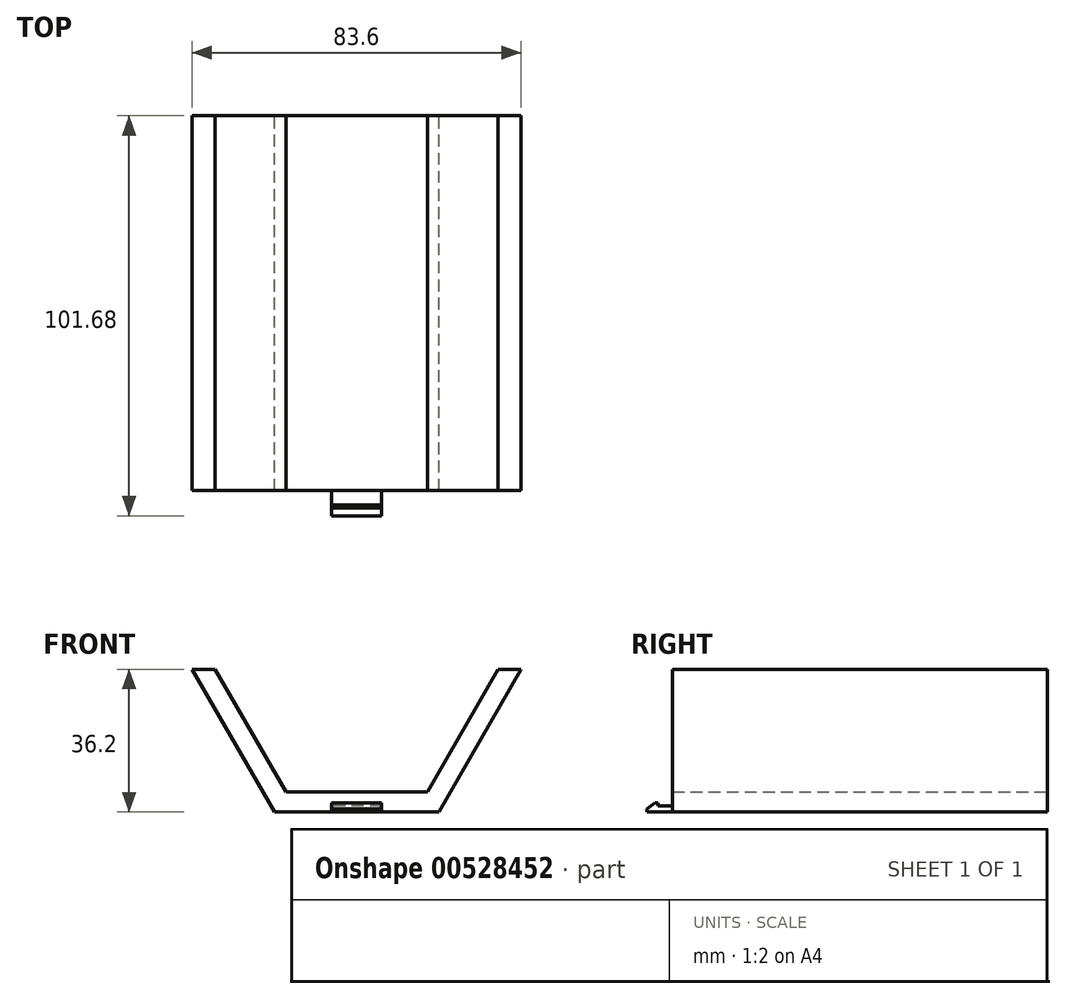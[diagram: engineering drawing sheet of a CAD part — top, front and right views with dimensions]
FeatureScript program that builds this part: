
annotation { "Feature Type Name" : "Feature", "Feature Type Description" : "" }
export const myFeature = defineFeature(function(context is Context, id is Id, definition is map)
    precondition{}
    {
        {
            var Q0;
            Q0=qCreatedBy(makeId("Front.planeOp"),FACE);
            var sketch = newSketch(context, id + "F0", { "sketchPlane" : qUnion([Q0])});
            skCircle(sketch, "E0.cCircle", {"center": v(0, 36.2) * mm, "radius": 36.2 * mm, "construction": true});
            skLineSegment(sketch, "E0.0", {"start": v(41.8, 36.2) * mm, "end": v(20.9, 0) * mm});
            skLineSegment(sketch, "E0.1", {"start": v(20.9, 0) * mm, "end": v(-20.9, 0) * mm});
            skLineSegment(sketch, "E0.2", {"start": v(-20.9, 0) * mm, "end": v(-41.8, 36.2) * mm});
            skLineSegment(sketch, "E0.3", {"start": v(-41.8, 36.2) * mm, "end": v(-20.9, 72.4) * mm, "construction": true});
            skLineSegment(sketch, "E0.4", {"start": v(-20.9, 72.4) * mm, "end": v(20.9, 72.4) * mm, "construction": true});
            skLineSegment(sketch, "E0.5", {"start": v(20.9, 72.39) * mm, "end": v(41.8, 36.2) * mm, "construction": true});
            skPoint(sketch, "E0.0.midPoint", {"position": v(31.35, 18.1) * mm});
            skLineSegment(sketch, "E1.0", {"start": v(-17.96, 5.08) * mm, "end": v(-35.93, 36.2) * mm});
            skLineSegment(sketch, "E1.1", {"start": v(-18.5, 67.31) * mm, "end": v(-17.96, 67.31) * mm});
            skLineSegment(sketch, "E1.2", {"start": v(17.7, 67.77) * mm, "end": v(17.96, 67.3) * mm});
            skLineSegment(sketch, "E1.3", {"start": v(-36.2, 35.74) * mm, "end": v(-35.93, 36.2) * mm});
            skLineSegment(sketch, "E1.4", {"start": v(35.93, 36.2) * mm, "end": v(17.96, 5.08) * mm});
            skLineSegment(sketch, "E1.5", {"start": v(17.96, 5.08) * mm, "end": v(-17.96, 5.08) * mm});
            skLineSegment(sketch, "E2", {"start": v(-35.93, 36.2) * mm, "end": v(-41.8, 36.2) * mm});
            skLineSegment(sketch, "E3", {"start": v(41.8, 36.2) * mm, "end": v(35.93, 36.2) * mm});
            skLineSegment(sketch, "E4.trimOffspring", {"start": v(35.93, 36.2) * mm, "end": v(36.2, 35.74) * mm});
            skLineSegment(sketch, "E5.trimOffspring", {"start": v(17.96, 67.31) * mm, "end": v(18.5, 67.31) * mm});
            skLineSegment(sketch, "E6.trimOffspring", {"start": v(-17.96, 67.31) * mm, "end": v(-17.7, 67.77) * mm});
            skSolve(sketch);
        }
        {
            var Q0;
            Q0 = qSketchRegion(id + "F0", true);
            extrude(context, id + "F1", {"entities" : qUnion([Q0]), "endBound" : BoundingType.SYMMETRIC, "depth" : 95.25 * mm, "offsetDistance" : 25.4 * mm});
        }
        {
            var Q0;
            Q0=qCreatedBy(makeId("Right.planeOp"),FACE);
            var sketch = newSketch(context, id + "F2", { "sketchPlane" : qUnion([Q0])});
            skLineSegment(sketch, "E7", {"start": v(-51.3, 1.52) * mm, "end": v(-51.3, 2.29) * mm});
            skLineSegment(sketch, "E8", {"start": v(-51.3, 2.29) * mm, "end": v(-52.07, 2.29) * mm});
            skLineSegment(sketch, "E9", {"start": v(-52.07, 2.29) * mm, "end": v(-54.06, 0.76) * mm});
            skLineSegment(sketch, "E10", {"start": v(-54.06, 0.76) * mm, "end": v(-54.06, 0) * mm});
            skLineSegment(sketch, "E11", {"start": v(-54.06, 0) * mm, "end": v(-47.63, 0) * mm});
            skLineSegment(sketch, "E12", {"start": v(-51.3, 1.52) * mm, "end": v(-51.3, 0) * mm, "construction": true});
            skLineSegment(sketch, "E13", {"start": v(-54.06, 0.76) * mm, "end": v(-52.07, 0.76) * mm, "construction": true});
            skLineSegment(sketch, "E14", {"start": v(-52.07, 0.76) * mm, "end": v(-52.07, 2.29) * mm, "construction": true});
            skLineSegment(sketch, "E15", {"start": v(-51.3, 1.52) * mm, "end": v(-47.63, 1.52) * mm});
            skLineSegment(sketch, "E16", {"start": v(-47.63, 1.52) * mm, "end": v(-47.63, 0) * mm});
            skSolve(sketch);
        }
        {
            var Q0;
            Q0 = qSketchRegion(id + "F2", true);
            extrude(context, id + "F3", {"entities" : qUnion([Q0]), "operationType" : NewBodyOperationType.ADD, "endBound" : BoundingType.SYMMETRIC, "depth" : 12.7 * mm, "offsetDistance" : 25.4 * mm});
        }
        {
            var Q0;
            Q0=makeQuery(id+"F3.opExtrude","CAP_EDGE",EDGE,{"disambiguationData":[OSD([sQuery(id+"F2.wireOp",EDGE,"E16")])],"isStart":true});
            var Q1;
            Q1=makeQuery(id+"F3.opExtrude","CAP_EDGE",EDGE,{"disambiguationData":[OSD([sQuery(id+"F2.wireOp",EDGE,"E16")])],"isStart":false});
            var Q2;
            Q2=makeQuery(id+"F3.opExtrude","SWEPT_EDGE",EDGE,{"disambiguationData":[OSD([sQuery(id+"F2.wireOp",EDGE,"E15"),sQuery(id+"F2.wireOp",EDGE,"E16")])]});
            fillet(context, id + "F4", {"entities" : qUnion([Q0, Q1, Q2]), "radius" : 0.5 * mm, "tangentPropagation" : true, "allowEdgeOverflow" : false});
        }
    });
